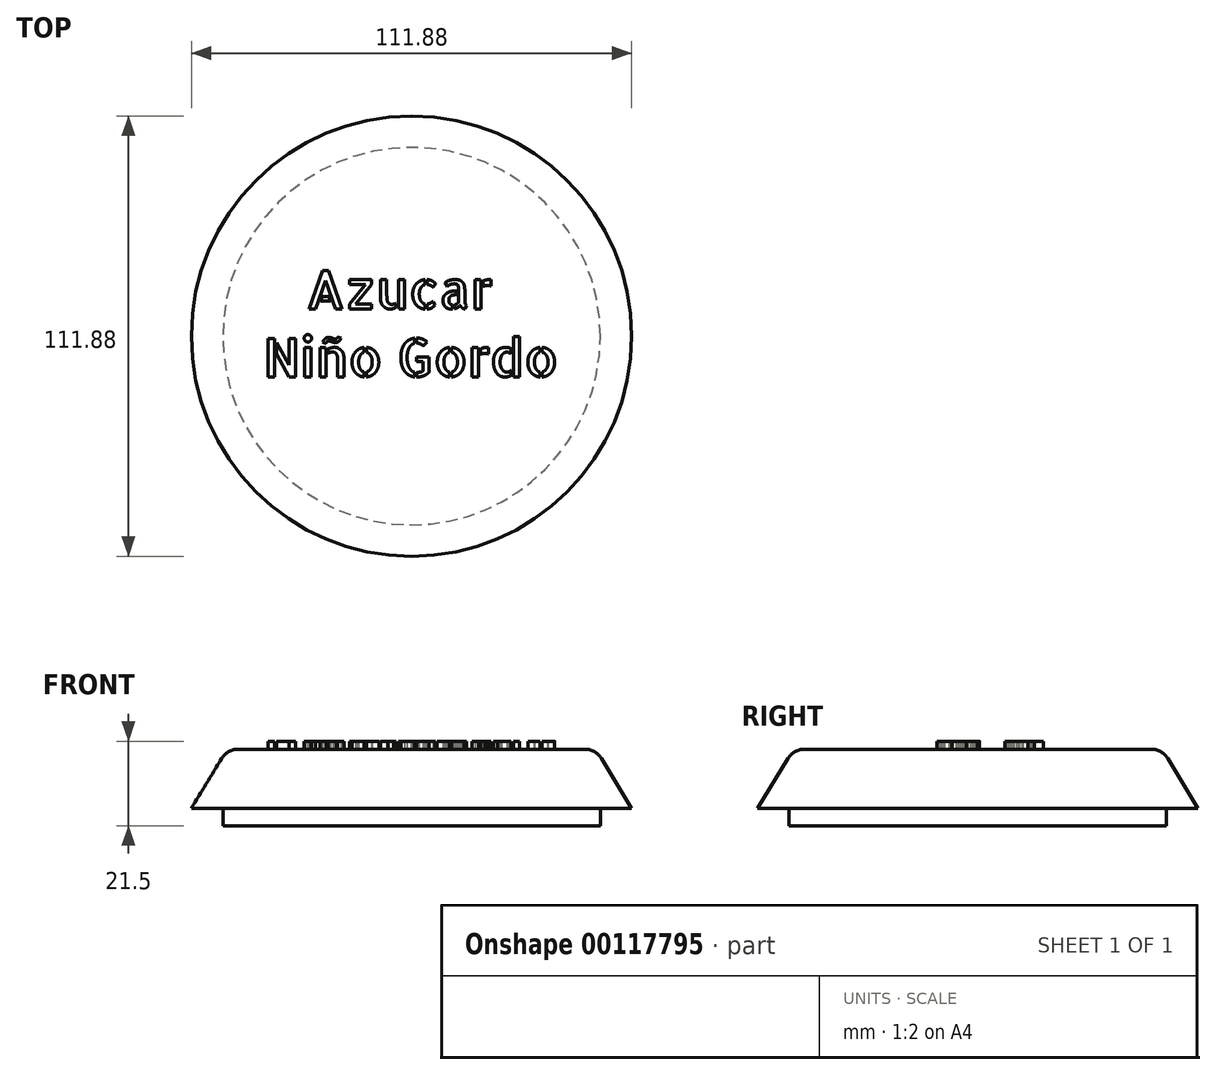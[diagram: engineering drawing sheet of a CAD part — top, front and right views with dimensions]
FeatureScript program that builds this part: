
annotation { "Feature Type Name" : "Feature", "Feature Type Description" : "" }
export const myFeature = defineFeature(function(context is Context, id is Id, definition is map)
    precondition{}
    {
        {
            var Q0;
            Q0=qCreatedBy(makeId("Front.planeOp"),FACE);
            var sketch = newSketch(context, id + "F0", { "sketchPlane" : qUnion([Q0])});
            skLineSegment(sketch, "E0", {"start": v(0, 0) * mm, "end": v(0, 15) * mm});
            skLineSegment(sketch, "E1", {"start": v(0, 15) * mm, "end": v(44, 15) * mm});
            skLineSegment(sketch, "E2", {"start": v(48.27, 12.6) * mm, "end": v(55.94, 0) * mm});
            skLineSegment(sketch, "E3", {"start": v(55.94, 0) * mm, "end": v(47.94, 0) * mm});
            skLineSegment(sketch, "E4", {"start": v(47.94, 0) * mm, "end": v(47.94, -4.5) * mm});
            skLineSegment(sketch, "E5", {"start": v(47.94, -4.5) * mm, "end": v(0, -4.5) * mm});
            skLineSegment(sketch, "E6", {"start": v(0, -4.5) * mm, "end": v(0, 0) * mm});
            skPoint(sketch, "E7.visualSharp", {"position": v(46.81, 15) * mm});
            skArc(sketch, "E7.filletArc", {"start": v(48.27, 12.6) * mm, "mid": v(46.45, 14.36) * mm, "end": v(44, 15) * mm});
            skSolve(sketch);
        }
        {
            var Q0;
            Q0 = qSketchRegion(id + "F0", true);
            var Q1;
            Q1=sQuery(id+"F0.wireOp",EDGE,"E0");
            revolve(context, id + "F1", {"entities" : qUnion([Q0]), "axis" : qUnion([Q1]), "revolveType" : RevolveType.FULL});
        }
        {
            var Q0;
            Q0=makeQuery(id+"F1.opRevolve","SWEPT_FACE",FACE,{"disambiguationData":[OSD([sQuery(id+"F0.wireOp",EDGE,"E1")])]});
            var sketch = newSketch(context, id + "F2", { "sketchPlane" : qUnion([Q0])});
            skText(sketch, "E8", { "text": "   Azucar\nNiño Gordo", "fontName": "AllertaStencil-Regular.ttf"});
            const initialGuessF2  = {"E8": [-0.03768, 0.00692, 1, 0, 0.0097]};
            skSetInitialGuess(sketch, initialGuessF2);
            skSolve(sketch);
        }
        {
            var Q0;
            Q0 = qSketchRegion(id + "F2", true);
            extrude(context, id + "F3", {"entities" : qUnion([Q0]), "operationType" : NewBodyOperationType.ADD, "depth" : 2 * mm});
        }
    });
